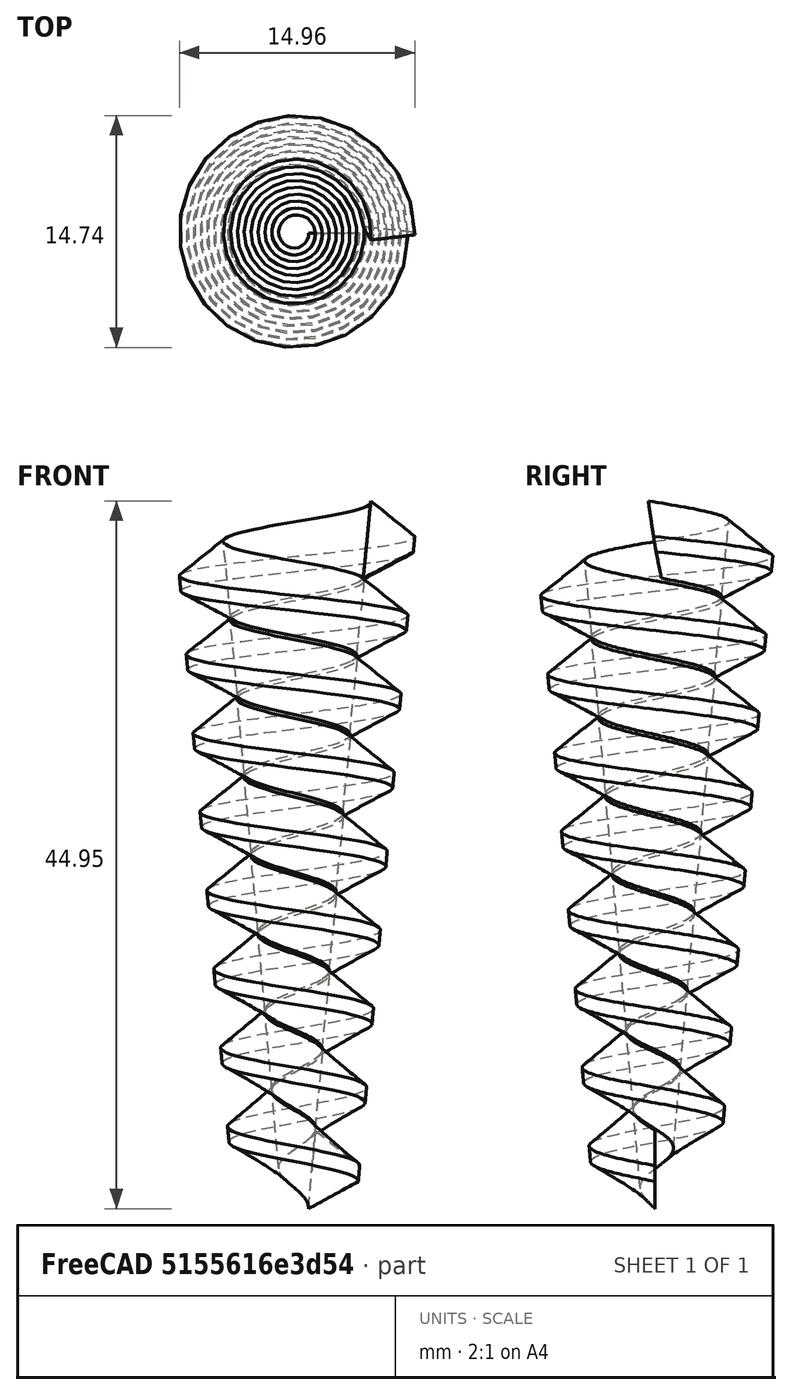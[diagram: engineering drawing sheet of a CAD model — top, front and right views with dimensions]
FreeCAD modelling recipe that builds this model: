
FCSTD DOCUMENT  (FreeCAD 0.16R6662 (Git))
Label: helix-and-profile-sweep
License: CreativeCommons Attribution-ShareAlike
LicenseURL: http://creativecommons.org/licenses/by-sa/4.0/
objects: Part::Helix×1, Sketcher::SketchObject×1, Part::Part2DObjectPython×1, Part::Sweep×1
note: 4 computed .brp shape members not serialized (recipe doc carries the construction recipe); baked Part::Feature solids carry a one-line shape summary decoded from their .brp

FEATURE [Part::Helix] Helix001
  Angle = 5
  Height = 40
  LocalCoord = 1
  Pitch = 5
  Radius = 2.6
  Style = 1
FEATURE [Sketcher::SketchObject] Sketch
  Placement = pos=(0,0,10) rot=(1,0,0;1.5708rad)
  sketch-geometry (4):
    g0: LineSegment StartX=-12 StartY=0 StartZ=0 EndX=-9 EndY=-2 EndZ=0
    g1: LineSegment StartX=-9 StartY=-2 StartZ=0 EndX=-9 EndY=3 EndZ=0
    g2: LineSegment StartX=-9 StartY=3 StartZ=0 EndX=-12 EndY=1 EndZ=0
    g3: LineSegment StartX=-12 StartY=1 StartZ=0 EndX=-12 EndY=0 EndZ=0
  constraints (7):
    c: PointOnObject(g0,g-1)
    c: Coincident(g0,g1)
    c: Vertical(g1)
    c: Coincident(g2,g3)
    c: Coincident(g3,g0)
    c: Vertical(g3)
    c: Coincident(g1,g2)
FEATURE [Part::Part2DObjectPython] DWire  # Draft 2D object (typed FeaturePython)
  Base = -> Sketch
  ChamferSize = 0
  Closed = true
  End = (0.832728,0,-2.23493)
  FilletRadius = 0
  Length = 18.5084
  MakeFace = true
  Placement = pos=(-7,0,11.5) rot=(0,1,0;3.22886rad)
  Points = (7) [(-9,2.07761e-16,10.9357),(-11,0,10),(-9,-2.22045e-16,9),(-9,-6.66134e-16,7),(-7,-6.66134e-16,7),(-7,6.66134e-16,13),(-9,6.66134e-16,13)]
  Start = (1.01265,0,-0.178461)
  Subdivisions = 0
FEATURE [Part::Sweep] Sweep
  Frenet = true
  Sections = -> [DWire]
  Solid = true
  Spine = -> Helix001
  Transition = 1
